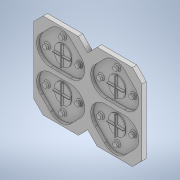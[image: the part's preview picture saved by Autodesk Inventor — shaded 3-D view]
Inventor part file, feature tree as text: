
AUTODESK INVENTOR PART (.ipt)
format: ipt  version: 2021 (Build 250183000, 183)  size: 420,864 bytes
history: native  units: mm
features: extrude x6, sketch x6, projected_geometry x3, mirror x2, chamfer x1, boolean_combine x1, pattern_linear x1, fillet x1
ambient origin geometry x8: Origin, YZ Plane, XZ Plane, XY Plane, X Axis, Y Axis, Z Axis, Center Point
bodies: Solid2 (feature_tree), Solid3 (feature_tree)
feature tree (21):
  extrude  "Extrusion3"  Depth=5.0mm
  extrude  "Extrusion4"  Depth=17.162mm
  chamfer  "Chamfer1"  Distance=1.5mm
  extrude  "Extrusion5"  Depth=1.5mm
  boolean_combine  "Combine1"
  mirror  "Mirror1"
  mirror  "Mirror2"
  extrude  "Extrusion8"  Depth=1.5mm
  pattern_linear  "Rectangular Pattern1"  Spacing1=4.0mm  [1 undecoded]
  extrude  "Extrusion6"  Depth=1.5mm
  fillet  "Fillet1"  Radius=4.0mm
  extrude  "Extrusion7"  Depth=2.0mm TaperAngle=0.0deg
  sketch  "Sketch1"  dims[d0=13.0mm d7=5.0mm]
  sketch  "Sketch4"  dims[d8=5.321mm d9=17.162mm]
  projected_geometry  "Projected Loop1"
  sketch  "Sketch5"  dims[d10=5.321mm]
  sketch  "Sketch6"  dims[d11=5.0mm]
  projected_geometry  "Projected Loop2"
  sketch  "Sketch7"  dims[d12=2.218mm]
  sketch  "Sketch8"  dims[d13=12.0mm d14=1.5mm d15=3.3mm d16=4.0mm d17=4.0mm d18=3.3mm d19=4.0mm d20=2.0mm d21=0.0mm d22=0.4mm d23=0.4mm d24=1.5mm d25=0.0mm d26=0.7mm d27=2.0mm d28=45.0deg d32=1.2mm d33=2.0mm d34=0.0mm d35=0.0mm d36=24.0mm d37=39.0mm d38=20.0mm d40=24.0mm d41=0.25mm d42=1.2mm d43=0.0mm d44=2.0mm d45=0.5mm d46=0.0mm d47=0.4mm d48=0.0mm d49=0.0mm d50=3.3mm d51=30.0mm d52=4.6mm d53=1.5mm]
  projected_geometry  "Projected Loop3"
note: 1 required parameter value undecoded (feature->parameter linkage not recoverable at this tier; creation-order binding heuristic only, values carry confidence <= 0.55)
